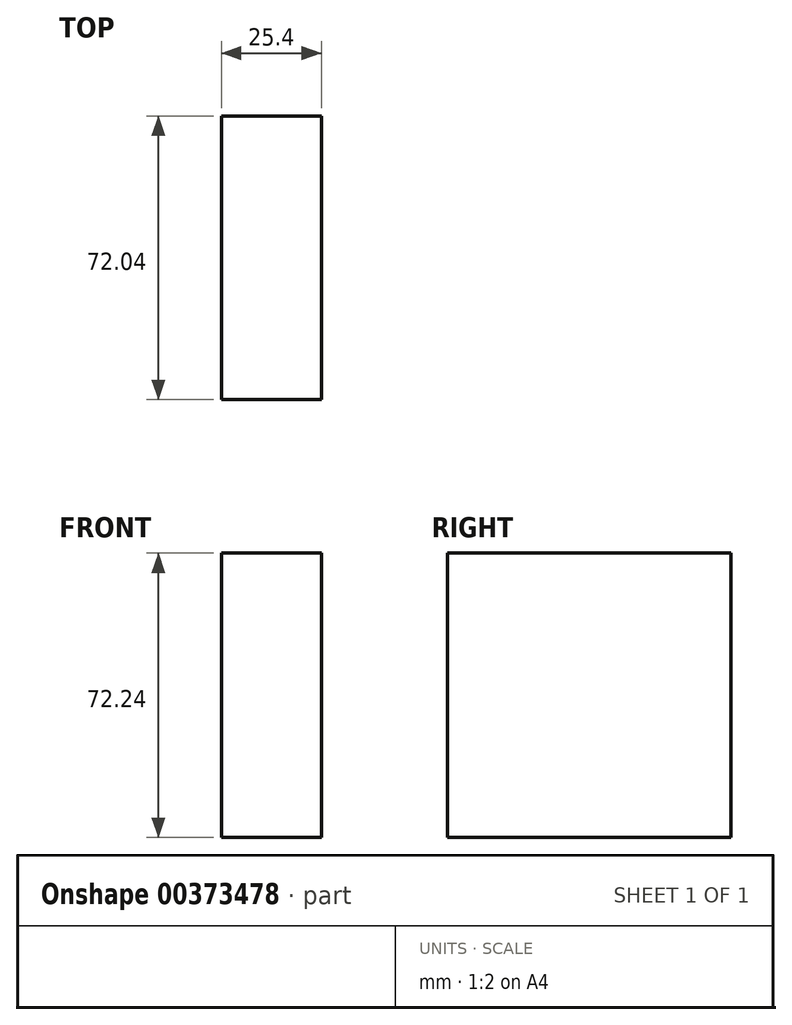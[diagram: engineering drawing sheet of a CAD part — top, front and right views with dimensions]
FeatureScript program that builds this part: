
annotation { "Feature Type Name" : "Feature", "Feature Type Description" : "" }
export const myFeature = defineFeature(function(context is Context, id is Id, definition is map)
    precondition{}
    {
        {
            var Q0;
            Q0=qCreatedBy(makeId("Right.planeOp"),FACE);
            var sketch = newSketch(context, id + "F0", { "sketchPlane" : qUnion([Q0])});
            skLineSegment(sketch, "E0.bottom", {"start": v(-23.46, 34.46) * mm, "end": v(48.58, 34.46) * mm});
            skLineSegment(sketch, "E0.top", {"start": v(-23.46, -37.78) * mm, "end": v(48.58, -37.78) * mm});
            skLineSegment(sketch, "E0.left", {"start": v(-23.46, 34.46) * mm, "end": v(-23.46, -37.78) * mm});
            skLineSegment(sketch, "E0.right", {"start": v(48.58, 34.46) * mm, "end": v(48.58, -37.78) * mm});
            skSolve(sketch);
        }
        {
            var Q0;
            Q0=makeQuery(id+"F0.imprint","IMPRINT",FACE,{"disambiguationData":[TD([[makeQuery(id+"F0.imprint","IMPRINT",EDGE,{"derivedFrom":sQuery(id+"F0.wireOp",EDGE,"E0.bottom")}),-1.0]])]});
            extrude(context, id + "F1", {"entities" : qUnion([Q0]), "depth" : 25.4 * mm});
        }
    });
